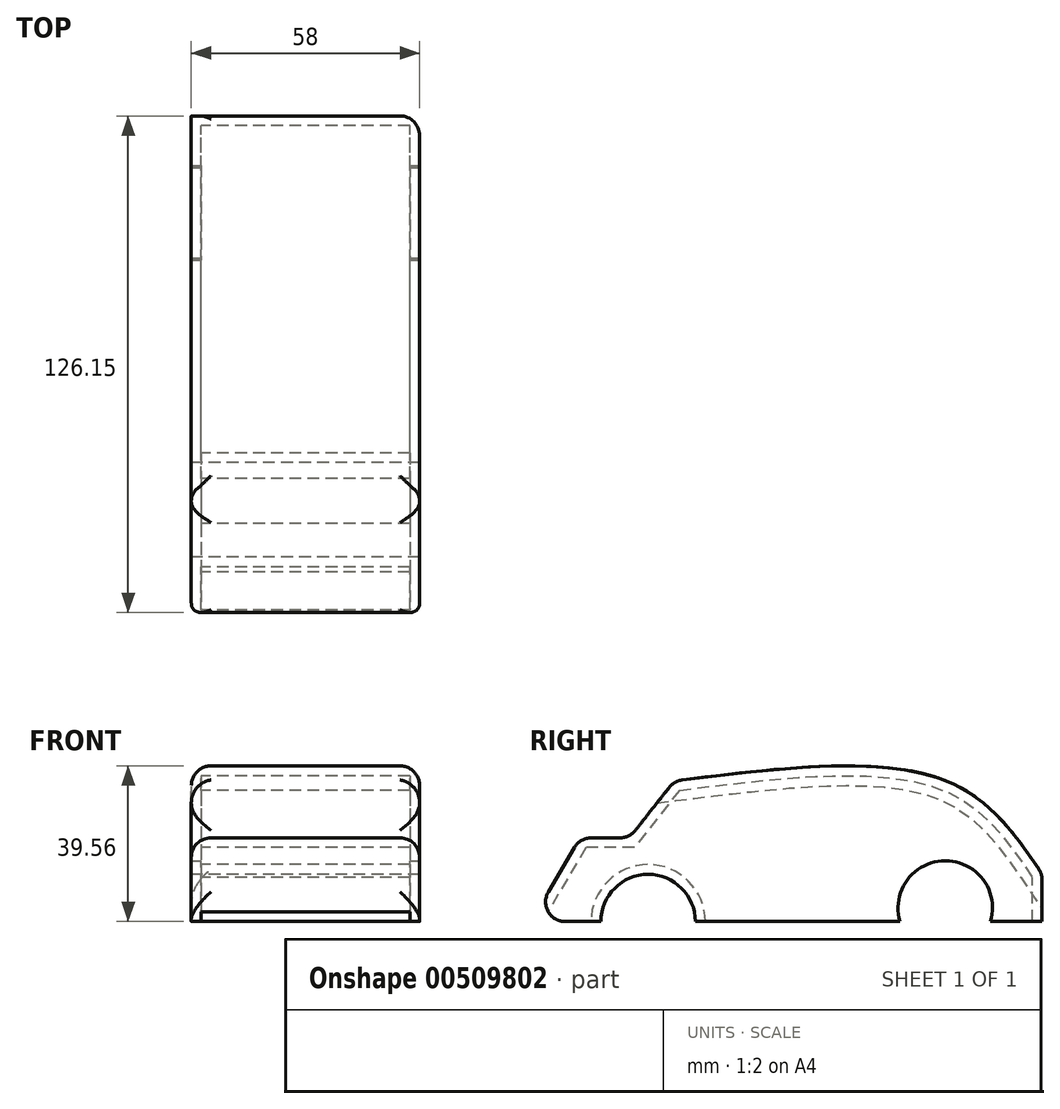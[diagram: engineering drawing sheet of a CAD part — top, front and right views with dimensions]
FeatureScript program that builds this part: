
annotation { "Feature Type Name" : "Feature", "Feature Type Description" : "" }
export const myFeature = defineFeature(function(context is Context, id is Id, definition is map)
    precondition{}
    {
        {
            var Q0;
            Q0=qCreatedBy(makeId("Top.planeOp"),FACE);
            cPlane(context, id + "F0", {"entities" : qUnion([Q0]), "cplaneType" : CPlaneType.OFFSET, "offset" : 3 * mm, "width" : 150 * mm, "height" : 150 * mm});
        }
        {
            var Q0;
            Q0=qCreatedBy(makeId("Right.planeOp"),FACE);
            var sketch = newSketch(context, id + "F1", { "sketchPlane" : qUnion([Q0])});
            skLineSegment(sketch, "E0", {"start": v(-70.51, 0) * mm, "end": v(59.39, 0) * mm});
            skLineSegment(sketch, "E1", {"start": v(59.39, 0) * mm, "end": v(59.39, 12.07) * mm});
            skLineSegment(sketch, "E2", {"start": v(-34.07, 35.73) * mm, "end": v(-45.43, 21.3) * mm});
            skLineSegment(sketch, "E3", {"start": v(-45.43, 21.3) * mm, "end": v(-57.97, 21.3) * mm});
            skLineSegment(sketch, "E4", {"start": v(-57.97, 21.3) * mm, "end": v(-70.51, 0) * mm});
            skCircle(sketch, "E5", {"center": v(-40.7, 0) * mm, "radius": 12 * mm});
            skCircle(sketch, "E6", {"center": v(30.52, 2) * mm, "radius": 12 * mm});
            skFitSpline(sketch, "E7", {"points": [v(-34.07, 35.73) * mm, v(35.1, 35.73) * mm, v(59.39, 12.07) * mm], "startDerivative": vector(134.86, 16.9) * mm, "endDerivative": vector(46.9, -69.3) * mm});
            skSolve(sketch);
        }
        {
            var Q0;
            {var subQ0=sQuery(id+"F1.wireOp",EDGE,"E1");Q0=makeQuery(id+"F1.imprint","IMPRINT",FACE,{"disambiguationData":[TD([[makeQuery(id+"F1.imprint","IMPRINT",EDGE,{"derivedFrom":subQ0}),1.0]])]});}
            var Q1;
            {var subQ0=sQuery(id+"F1.wireOp",EDGE,"E6");var subQ1=sQuery(id+"F1.wireOp",EDGE,"E0");var subQ2=makeQuery(id+"F1.imprint","INTERSECT",VERTEX,{"disambiguationData":[OD(0.0)],"derivedFrom":[subQ1,subQ0]});Q1=makeQuery(id+"F1.imprint","IMPRINT",FACE,{"disambiguationData":[TD([[makeQuery(id+"F1.imprint","IMPRINT",EDGE,{"disambiguationData":[TD([[subQ2,-1.0]])],"derivedFrom":subQ1}),1.0]])]});}
            var Q2;
            {var subQ0=sQuery(id+"F1.wireOp",EDGE,"E5");var subQ1=sQuery(id+"F1.wireOp",EDGE,"E0");var subQ2=makeQuery(id+"F1.imprint","INTERSECT",VERTEX,{"disambiguationData":[OD(0.0)],"derivedFrom":[subQ1,subQ0]});Q2=makeQuery(id+"F1.imprint","IMPRINT",FACE,{"disambiguationData":[TD([[makeQuery(id+"F1.imprint","IMPRINT",EDGE,{"disambiguationData":[TD([[subQ2,-1.0]])],"derivedFrom":subQ1}),1.0]])]});}
            extrude(context, id + "F2", {"entities" : qUnion([Q0, Q1, Q2]), "endBound" : BoundingType.SYMMETRIC, "depth" : 58 * mm});
        }
        {
            var Q0;
            Q0=makeQuery(id+"F2.opExtrude","SWEPT_FACE",FACE,{"disambiguationData":[OSD([sQuery(id+"F1.wireOp",EDGE,"E0")])]});
            shell(context, id + "F3", {"entities" : qUnion([Q0]), "thickness" : 2.5 * mm});
        }
        {
            var Q0;
            Q0=makeQuery(id+"F2.opExtrude","SWEPT_EDGE",EDGE,{"disambiguationData":[OSD([sQuery(id+"F1.wireOp",EDGE,"E2"),sQuery(id+"F1.wireOp",EDGE,"E7")])]});
            var Q1;
            Q1=makeQuery(id+"F2.opExtrude","SWEPT_EDGE",EDGE,{"disambiguationData":[OSD([sQuery(id+"F1.wireOp",EDGE,"E2"),sQuery(id+"F1.wireOp",EDGE,"E3")])]});
            var Q2;
            Q2=makeQuery(id+"F2.opExtrude","SWEPT_EDGE",EDGE,{"disambiguationData":[OSD([sQuery(id+"F1.wireOp",EDGE,"E3"),sQuery(id+"F1.wireOp",EDGE,"E4")])]});
            var Q3;
            Q3=makeQuery(id+"F2.opExtrude","CAP_EDGE",EDGE,{"disambiguationData":[OSD([sQuery(id+"F1.wireOp",EDGE,"E7")])],"isStart":false});
            var Q4;
            Q4=makeQuery(id+"F2.opExtrude","SWEPT_FACE",FACE,{"disambiguationData":[OSD([sQuery(id+"F1.wireOp",EDGE,"E7")])]});
            var Q5;
            Q5=makeQuery(id+"F2.opExtrude","CAP_EDGE",EDGE,{"disambiguationData":[OSD([sQuery(id+"F1.wireOp",EDGE,"E7")])],"isStart":true});
            var Q6;
            Q6=makeQuery(id+"F2.opExtrude","CAP_EDGE",EDGE,{"disambiguationData":[OSD([sQuery(id+"F1.wireOp",EDGE,"E1")])],"isStart":false});
            var Q7;
            Q7=makeQuery(id+"F2.opExtrude","SWEPT_FACE",FACE,{"disambiguationData":[OSD([sQuery(id+"F1.wireOp",EDGE,"E4")])]});
            var Q8;
            Q8=makeQuery(id+"F2.opExtrude","CAP_EDGE",EDGE,{"disambiguationData":[OSD([sQuery(id+"F1.wireOp",EDGE,"E3")])],"isStart":false});
            var Q9;
            Q9=makeQuery(id+"F2.opExtrude","CAP_EDGE",EDGE,{"disambiguationData":[OSD([sQuery(id+"F1.wireOp",EDGE,"E3")])],"isStart":true});
            fillet(context, id + "F4", {"entities" : qUnion([Q0, Q1, Q2, Q3, Q4, Q5, Q6, Q7, Q8, Q9]), "radius" : 5 * mm, "tangentPropagation" : true, "allowEdgeOverflow" : false});
        }
        {
            var Q0;
            Q0=makeQuery(id+"F2.opExtrude","CAP_FACE",FACE,{"disambiguationData":[OSD([sQuery(id+"F1.wireOp",EDGE,"E0"),sQuery(id+"F1.wireOp",EDGE,"E1"),sQuery(id+"F1.wireOp",EDGE,"E2"),sQuery(id+"F1.wireOp",EDGE,"E3"),sQuery(id+"F1.wireOp",EDGE,"E4"),sQuery(id+"F1.wireOp",EDGE,"E7")])],"isStart":false});
            var sketch = newSketch(context, id + "F5", { "sketchPlane" : qUnion([Q0])});
            skCircle(sketch, "E8", {"center": v(-36.43, 0) * mm, "radius": 12 * mm});
            skCircle(sketch, "E9", {"center": v(34.8, 3.47) * mm, "radius": 12 * mm});
            skSolve(sketch);
        }
        {
            var Q0;
            {var subQ0=sQuery(id+"F5.wireOp",EDGE,"E8");var subQ1=makeQuery(id+"F2.opExtrude","CAP_EDGE",EDGE,{"disambiguationData":[OSD([sQuery(id+"F1.wireOp",EDGE,"E0")])],"isStart":false});var subQ2=makeQuery(id+"F5.imprint","INTERSECT",VERTEX,{"disambiguationData":[OD(0.0)],"derivedFrom":[subQ1,subQ0]});Q0=makeQuery(id+"F5.imprint","IMPRINT",FACE,{"disambiguationData":[TD([[makeQuery(id+"F5.imprint","IMPRINT",EDGE,{"disambiguationData":[TD([[subQ2,1.0]])],"derivedFrom":subQ0}),1.0]])]});}
            var Q1;
            {var subQ0=sQuery(id+"F5.wireOp",EDGE,"E9");var subQ1=makeQuery(id+"F2.opExtrude","CAP_EDGE",EDGE,{"disambiguationData":[OSD([sQuery(id+"F1.wireOp",EDGE,"E0")])],"isStart":false});var subQ2=makeQuery(id+"F5.imprint","INTERSECT",VERTEX,{"disambiguationData":[OD(0.0)],"derivedFrom":[subQ1,subQ0]});Q1=makeQuery(id+"F5.imprint","IMPRINT",FACE,{"disambiguationData":[TD([[makeQuery(id+"F5.imprint","IMPRINT",EDGE,{"disambiguationData":[TD([[subQ2,-1.0]])],"derivedFrom":subQ0}),1.0]])]});}
            extrude(context, id + "F6", {"entities" : qUnion([Q0, Q1]), "operationType" : NewBodyOperationType.REMOVE, "oppositeDirection" : true, "depth" : 60 * mm});
        }
    });
